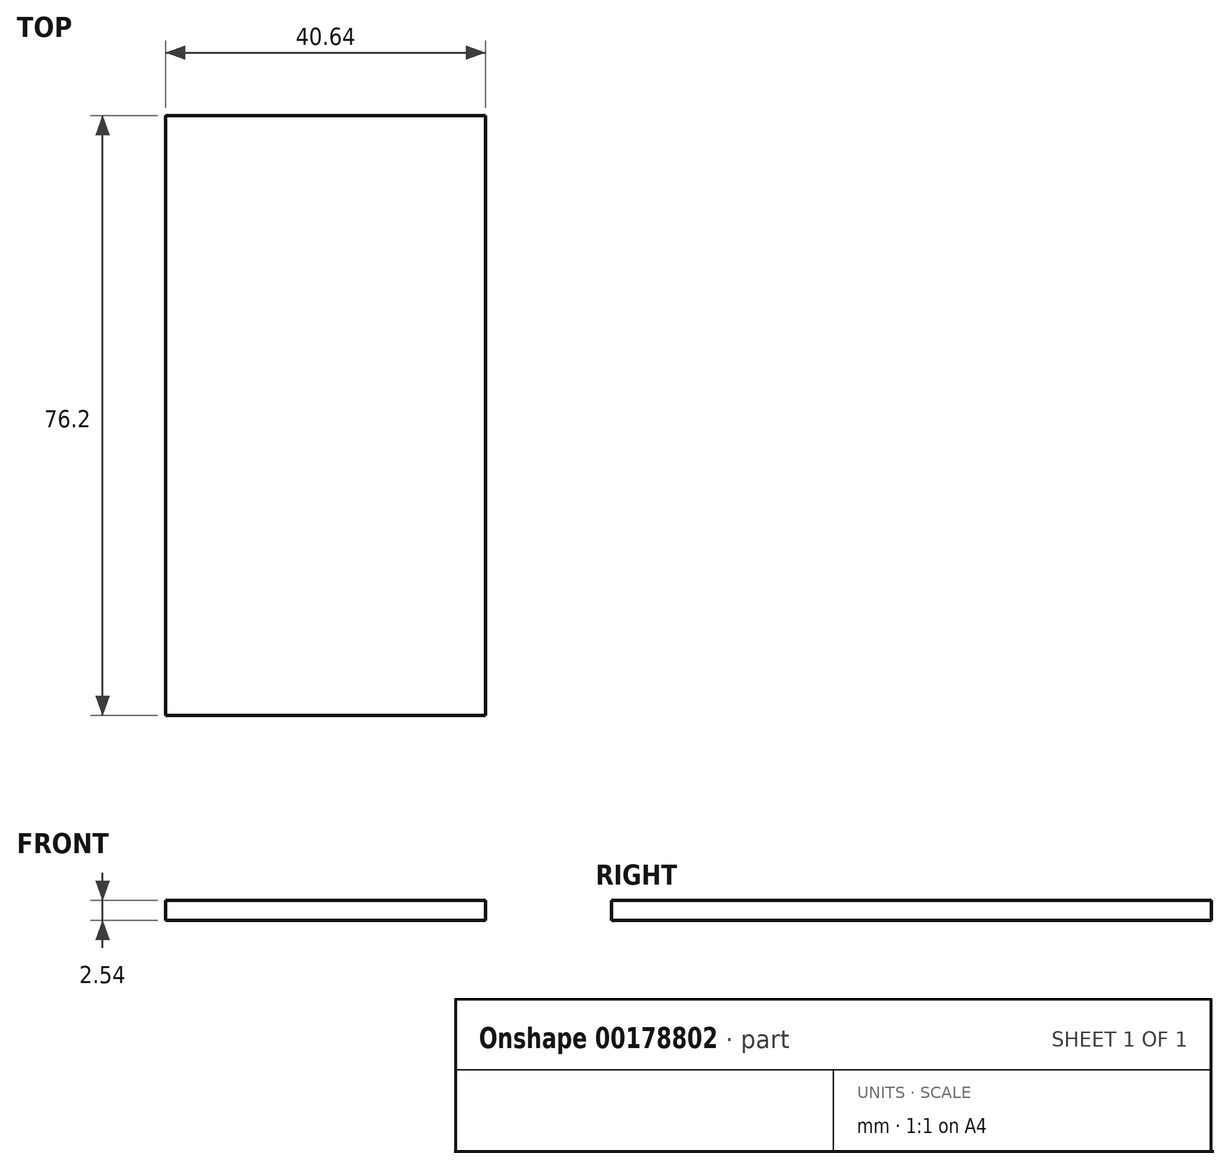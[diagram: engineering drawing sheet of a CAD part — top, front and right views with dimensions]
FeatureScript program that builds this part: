
annotation { "Feature Type Name" : "Feature", "Feature Type Description" : "" }
export const myFeature = defineFeature(function(context is Context, id is Id, definition is map)
    precondition{}
    {
        {
            var Q0;
            Q0=qCreatedBy(makeId("Top.planeOp"),FACE);
            var sketch = newSketch(context, id + "F0", { "sketchPlane" : qUnion([Q0])});
            skLineSegment(sketch, "E0.bottom", {"start": v(0, 0) * mm, "end": v(-40.64, 0) * mm});
            skLineSegment(sketch, "E0.top", {"start": v(0, 76.2) * mm, "end": v(-40.64, 76.2) * mm});
            skLineSegment(sketch, "E0.left", {"start": v(0, 0) * mm, "end": v(0, 76.2) * mm});
            skLineSegment(sketch, "E0.right", {"start": v(-40.64, 0) * mm, "end": v(-40.64, 76.2) * mm});
            skSolve(sketch);
        }
        {
            var Q0;
            Q0=makeQuery(id+"F0.imprint","IMPRINT",FACE,{"disambiguationData":[TD([[makeQuery(id+"F0.imprint","IMPRINT",EDGE,{"derivedFrom":sQuery(id+"F0.wireOp",EDGE,"E0.bottom")}),-1.0]])]});
            extrude(context, id + "F1", {"entities" : qUnion([Q0]), "depth" : 2.54 * mm});
        }
    });
